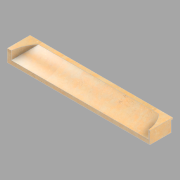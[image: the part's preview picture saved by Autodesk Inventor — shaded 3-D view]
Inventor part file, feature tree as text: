
AUTODESK INVENTOR PART (.ipt)
format: ipt  version: 2022.2 (Build 262287010, 287A)  size: 134,656 bytes
history: native  units: in
note: dims shown in document units (in); Inventor stores cm internally (conversion verified against a paired STEP export)
features: other x1, direct_edit x1, revolve x1
ambient origin geometry x8: Origin, YZ Plane, XZ Plane, XY Plane, X Axis, Y Axis, Z Axis, Center Point
bodies: Solid1 (feature_tree)
feature tree (3):
  other  "North (4) (2)"
  direct_edit  "Direct Edit1"
  revolve  "Rotate1"  Angle=90.0deg
